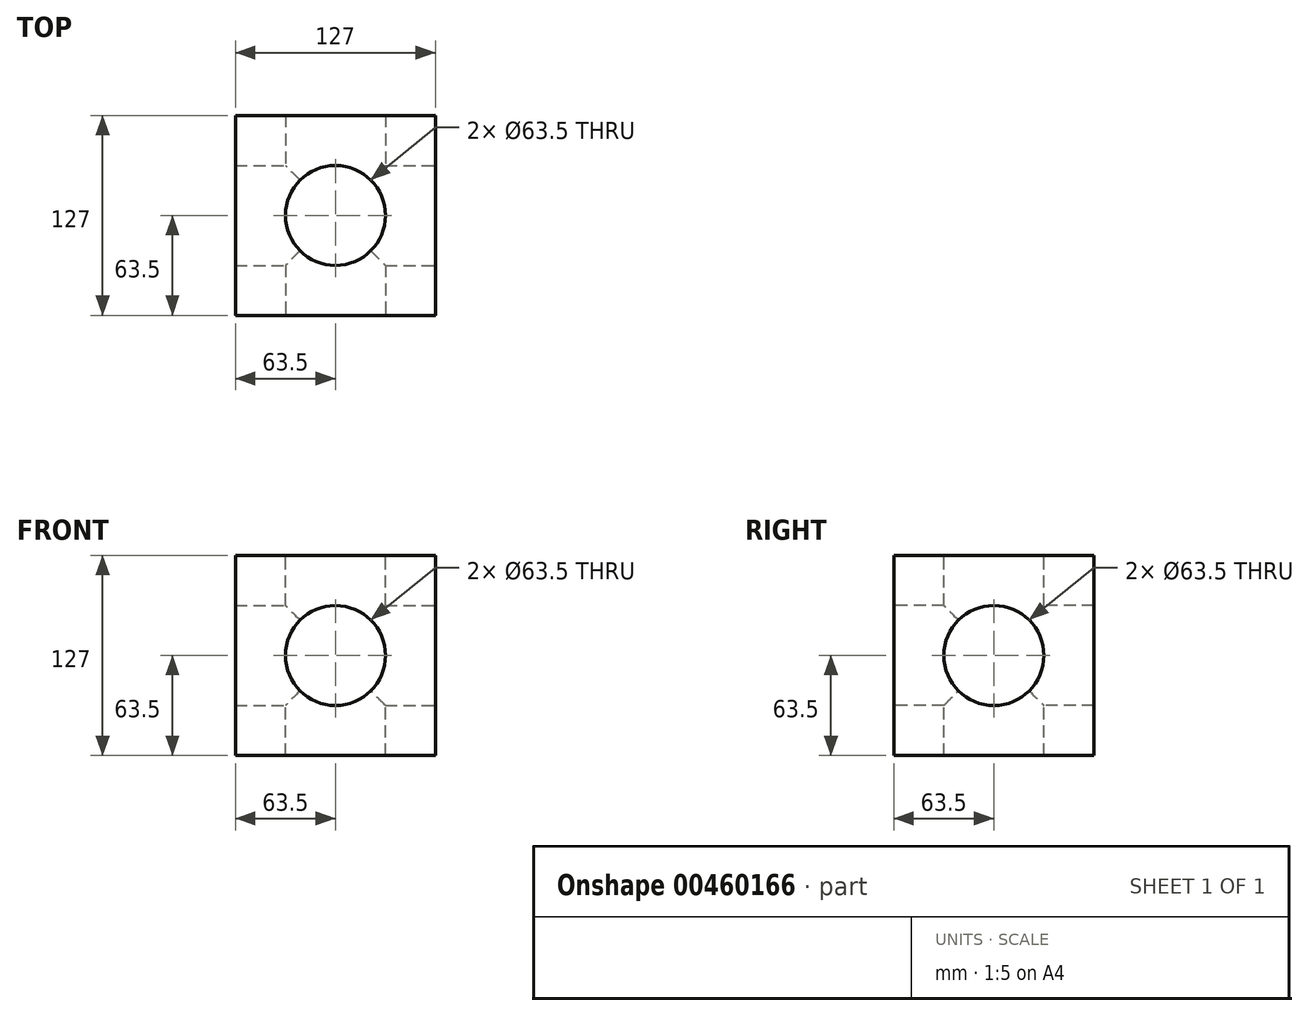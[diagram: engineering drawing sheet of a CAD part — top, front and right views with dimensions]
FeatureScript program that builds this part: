
annotation { "Feature Type Name" : "Feature", "Feature Type Description" : "" }
export const myFeature = defineFeature(function(context is Context, id is Id, definition is map)
    precondition{}
    {
        {
            var Q0;
            Q0=qCreatedBy(makeId("Top.planeOp"),FACE);
            var sketch = newSketch(context, id + "F0", { "sketchPlane" : qUnion([Q0])});
            skLineSegment(sketch, "E0.bottom", {"start": v(-63.5, -63.5) * mm, "end": v(63.5, -63.5) * mm});
            skLineSegment(sketch, "E0.top", {"start": v(-63.5, 63.5) * mm, "end": v(63.5, 63.5) * mm});
            skLineSegment(sketch, "E0.left", {"start": v(-63.5, -63.5) * mm, "end": v(-63.5, 63.5) * mm});
            skLineSegment(sketch, "E0.right", {"start": v(63.5, -63.5) * mm, "end": v(63.5, 63.5) * mm});
            skLineSegment(sketch, "E1", {"start": v(-63.5, 0) * mm, "end": v(0, 0) * mm});
            skLineSegment(sketch, "E2", {"start": v(63.5, 0) * mm, "end": v(0, 0) * mm});
            skLineSegment(sketch, "E3", {"start": v(0, 0) * mm, "end": v(0, 63.5) * mm});
            skLineSegment(sketch, "E4", {"start": v(0, 0) * mm, "end": v(0, -63.5) * mm});
            skSolve(sketch);
        }
        {
            var Q0;
            {var subQ4=sQuery(id+"F0.wireOp",EDGE,"E1");Q0=makeQuery(id+"F0.imprint","IMPRINT",FACE,{"disambiguationData":[TD([[makeQuery(id+"F0.imprint","IMPRINT",EDGE,{"derivedFrom":subQ4}),1.0]])]});}
            var Q1;
            Q1 = qSketchRegion(id + "F0", true);
            extrude(context, id + "F1", {"entities" : qUnion([Q0, Q1]), "endBound" : BoundingType.SYMMETRIC, "depth" : 127 * mm});
        }
        {
            var Q0;
            Q0=makeQuery(id+"F1.opExtrude","SWEPT_FACE",FACE,{"disambiguationData":[OSD([sQuery(id+"F0.wireOp",EDGE,"E0.right")])]});
            var sketch = newSketch(context, id + "F2", { "sketchPlane" : qUnion([Q0])});
            skCircle(sketch, "E5", {"center": v(0, 0) * mm, "radius": 31.75 * mm});
            skSolve(sketch);
        }
        {
            var Q0;
            Q0 = qSketchRegion(id + "F2", true);
            extrude(context, id + "F3", {"entities" : qUnion([Q0]), "operationType" : NewBodyOperationType.REMOVE, "endBound" : BoundingType.THROUGH_ALL, "oppositeDirection" : true, "depth" : 25.4 * mm});
        }
        {
            var Q0;
            Q0=makeQuery(id+"F1.opExtrude","SWEPT_FACE",FACE,{"disambiguationData":[OSD([sQuery(id+"F0.wireOp",EDGE,"E0.bottom")])]});
            var sketch = newSketch(context, id + "F4", { "sketchPlane" : qUnion([Q0])});
            skCircle(sketch, "E6", {"center": v(0, 0) * mm, "radius": 31.75 * mm});
            skSolve(sketch);
        }
        {
            var Q0;
            Q0 = qSketchRegion(id + "F4", true);
            extrude(context, id + "F5", {"entities" : qUnion([Q0]), "operationType" : NewBodyOperationType.REMOVE, "endBound" : BoundingType.THROUGH_ALL, "oppositeDirection" : true, "depth" : 25.4 * mm});
        }
        {
            var Q0;
            Q0=makeQuery(id+"F1.opExtrude","CAP_FACE",FACE,{"disambiguationData":[OSD([sQuery(id+"F0.wireOp",EDGE,"E0.bottom"),sQuery(id+"F0.wireOp",EDGE,"E0.top"),sQuery(id+"F0.wireOp",EDGE,"E0.left"),sQuery(id+"F0.wireOp",EDGE,"E0.right")])],"isStart":false});
            var sketch = newSketch(context, id + "F6", { "sketchPlane" : qUnion([Q0])});
            skCircle(sketch, "E7", {"center": v(0, 0) * mm, "radius": 31.75 * mm});
            skSolve(sketch);
        }
        {
            var Q0;
            Q0 = qSketchRegion(id + "F6", true);
            extrude(context, id + "F7", {"entities" : qUnion([Q0]), "operationType" : NewBodyOperationType.REMOVE, "endBound" : BoundingType.THROUGH_ALL, "oppositeDirection" : true, "depth" : 25.4 * mm});
        }
    });
